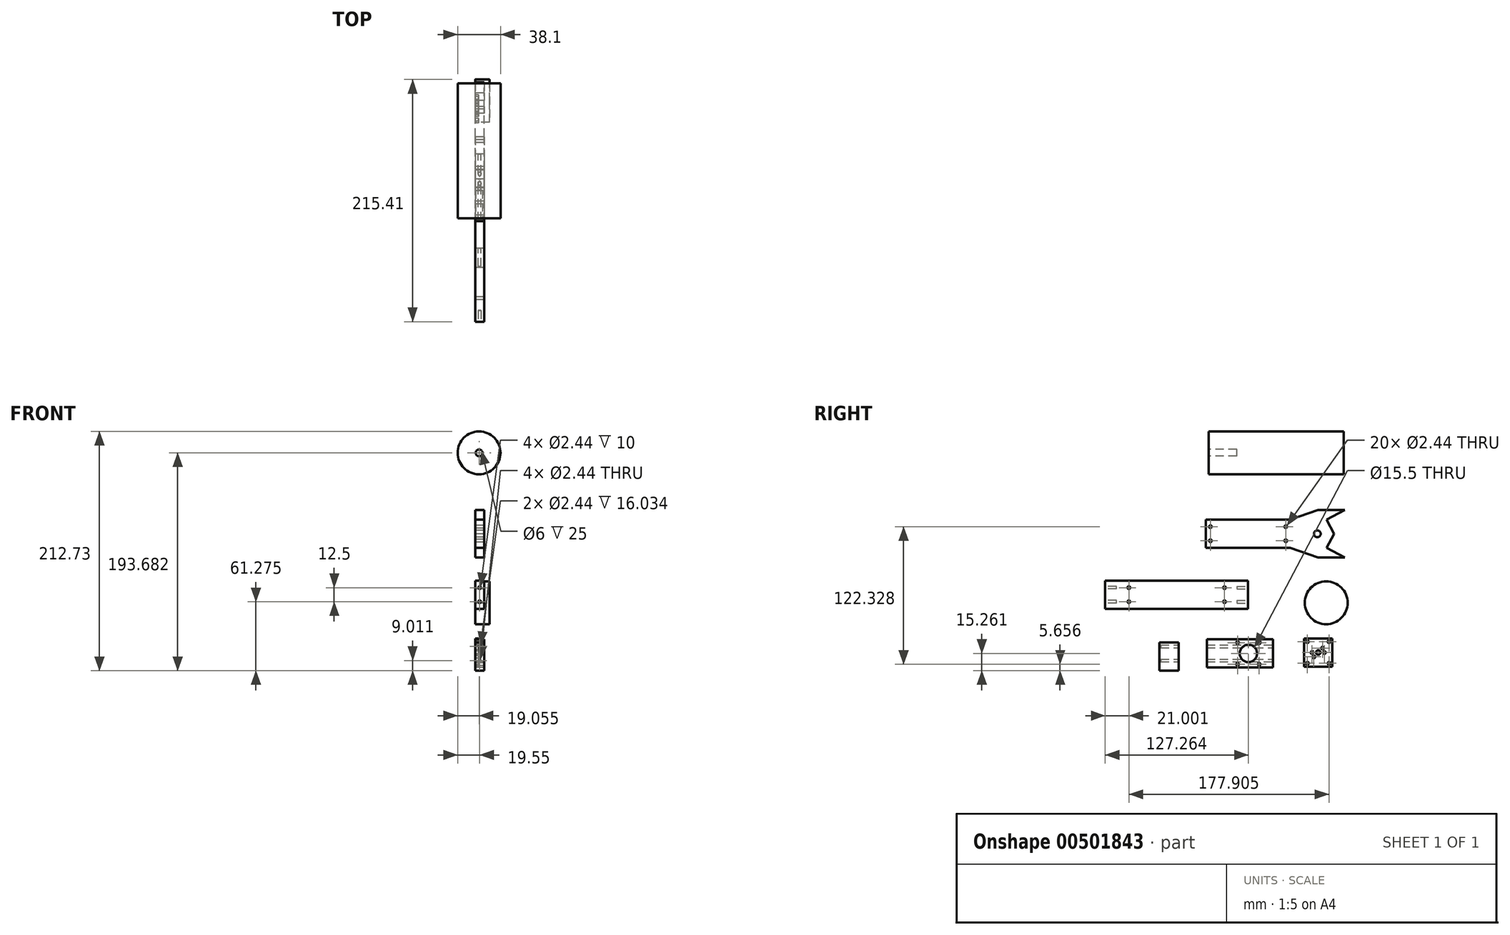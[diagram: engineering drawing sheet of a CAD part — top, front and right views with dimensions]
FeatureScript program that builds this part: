
annotation { "Feature Type Name" : "Feature", "Feature Type Description" : "" }
export const myFeature = defineFeature(function(context is Context, id is Id, definition is map)
    precondition{}
    {
        {
            var Q0;
            Q0=qCreatedBy(makeId("Right.planeOp"),FACE);
            var sketch = newSketch(context, id + "F0", { "sketchPlane" : qUnion([Q0])});
            skLineSegment(sketch, "E0", {"start": v(-2.43, 11.31) * mm, "end": v(-2.43, -13.69) * mm});
            skLineSegment(sketch, "E1", {"start": v(-2.43, -13.69) * mm, "end": v(72.57, -13.69) * mm});
            skLineSegment(sketch, "E2", {"start": v(72.57, 11.31) * mm, "end": v(-2.43, 11.31) * mm});
            skCircle(sketch, "E3", {"center": v(1.57, 5.06) * mm, "radius": 1.22 * mm});
            skCircle(sketch, "E4", {"center": v(1.57, -7.44) * mm, "radius": 1.22 * mm});
            skCircle(sketch, "E5", {"center": v(68.57, 5.06) * mm, "radius": 1.22 * mm});
            skCircle(sketch, "E6", {"center": v(68.57, -7.44) * mm, "radius": 1.22 * mm});
            skCircle(sketch, "E7", {"center": v(96.58, -1.29) * mm, "radius": 3 * mm});
            skLineSegment(sketch, "E8", {"start": v(120.9, 31.46) * mm, "end": v(120.9, -36.2) * mm});
            skLineSegment(sketch, "E9", {"start": v(72.57, 11.31) * mm, "end": v(97.18, 19.85) * mm});
            skLineSegment(sketch, "E10", {"start": v(72.57, -13.69) * mm, "end": v(97.22, -22.36) * mm});
            skLineSegment(sketch, "E11", {"start": v(97.18, 19.85) * mm, "end": v(120.9, 19.85) * mm});
            skLineSegment(sketch, "E12", {"start": v(97.22, -22.36) * mm, "end": v(120.9, -22.36) * mm});
            skLineSegment(sketch, "E13", {"start": v(120.9, 19.85) * mm, "end": v(104.74, 11.3) * mm});
            skLineSegment(sketch, "E14", {"start": v(104.74, 11.3) * mm, "end": v(111.58, -1.29) * mm});
            skLineSegment(sketch, "E15", {"start": v(120.9, -22.36) * mm, "end": v(104.74, -13.78) * mm});
            skLineSegment(sketch, "E16", {"start": v(111.58, -1.29) * mm, "end": v(104.74, -13.78) * mm});
            skSolve(sketch);
        }
        {
            var Q0;
            Q0=makeQuery(id+"F0.imprint","IMPRINT",FACE,{"disambiguationData":[TD([[makeQuery(id+"F0.imprint","IMPRINT",EDGE,{"derivedFrom":sQuery(id+"F0.wireOp",EDGE,"E0")}),1.0]])]});
            var Q1;
            Q1=makeQuery(id+"F0.imprint","IMPRINT",FACE,{"disambiguationData":[TD([[makeQuery(id+"F0.imprint","IMPRINT",EDGE,{"derivedFrom":sQuery(id+"F0.wireOp",EDGE,"7be34ed3-0eaf-4511-ae4f-23863d348a8b")}),1.0]])]});
            extrude(context, id + "F1", {"entities" : qUnion([Q0, Q1]), "depth" : 8 * mm});
        }
        {
            var Q0;
            Q0=qCreatedBy(makeId("Right.planeOp"),FACE);
            var sketch = newSketch(context, id + "F2", { "sketchPlane" : qUnion([Q0])});
            skLineSegment(sketch, "E17", {"start": v(-91.93, -42.9) * mm, "end": v(-91.93, -67.9) * mm});
            skLineSegment(sketch, "E18", {"start": v(-91.93, -42.9) * mm, "end": v(35.07, -42.9) * mm});
            skLineSegment(sketch, "E19", {"start": v(35.07, -42.9) * mm, "end": v(35.07, -67.9) * mm});
            skLineSegment(sketch, "E20", {"start": v(35.07, -67.9) * mm, "end": v(-91.93, -67.9) * mm});
            skCircle(sketch, "E21", {"center": v(-70.93, -49.14) * mm, "radius": 1.22 * mm});
            skCircle(sketch, "E22", {"center": v(-70.93, -61.64) * mm, "radius": 1.22 * mm});
            skPoint(sketch, "E23.endSnap0", {"position": v(35.07, -55.4) * mm});
            skCircle(sketch, "E24", {"center": v(14.07, -49.14) * mm, "radius": 1.22 * mm});
            skCircle(sketch, "E25", {"center": v(14.07, -61.64) * mm, "radius": 1.22 * mm});
            skSolve(sketch);
        }
        {
            var Q0;
            Q0=makeQuery(id+"F2.imprint","IMPRINT",FACE,{"disambiguationData":[TD([[makeQuery(id+"F2.imprint","IMPRINT",EDGE,{"derivedFrom":sQuery(id+"F2.wireOp",EDGE,"E17")}),1.0]])]});
            extrude(context, id + "F3", {"entities" : qUnion([Q0]), "depth" : 8 * mm});
        }
        {
            var Q0;
            Q0=qCreatedBy(makeId("Right.planeOp"),FACE);
            var sketch = newSketch(context, id + "F4", { "sketchPlane" : qUnion([Q0])});
            skCircle(sketch, "E26", {"center": v(104.43, -62.58) * mm, "radius": 19.05 * mm});
            skSolve(sketch);
        }
        {
            var Q0;
            Q0=makeQuery(id+"F4.imprint","IMPRINT",FACE,{"disambiguationData":[TD([[makeQuery(id+"F4.imprint","IMPRINT",EDGE,{"derivedFrom":sQuery(id+"F4.wireOp",EDGE,"E26")}),1.0]])]});
            extrude(context, id + "F5", {"entities" : qUnion([Q0]), "depth" : 12.7 * mm});
        }
        {
            var Q0;
            Q0=qCreatedBy(makeId("Right.planeOp"),FACE);
            var sketch = newSketch(context, id + "F6", { "sketchPlane" : qUnion([Q0])});
            skLineSegment(sketch, "E27", {"start": v(-43.63, -97.92) * mm, "end": v(-43.63, -122.92) * mm});
            skLineSegment(sketch, "E28", {"start": v(-43.63, -122.92) * mm, "end": v(-26.63, -122.92) * mm});
            skLineSegment(sketch, "E29", {"start": v(-26.63, -122.92) * mm, "end": v(-26.63, -97.92) * mm});
            skLineSegment(sketch, "E30", {"start": v(-26.63, -97.92) * mm, "end": v(-43.63, -97.92) * mm});
            skSolve(sketch);
        }
        {
            var Q0;
            Q0=qCreatedBy(makeId("Right.planeOp"),FACE);
            var sketch = newSketch(context, id + "F7", { "sketchPlane" : qUnion([Q0])});
            skLineSegment(sketch, "E31", {"start": v(-1.67, -95.16) * mm, "end": v(-1.67, -120.16) * mm});
            skLineSegment(sketch, "E32", {"start": v(-1.67, -120.16) * mm, "end": v(57.33, -120.16) * mm});
            skLineSegment(sketch, "E33", {"start": v(57.33, -120.16) * mm, "end": v(57.33, -95.16) * mm});
            skLineSegment(sketch, "E34", {"start": v(57.33, -95.16) * mm, "end": v(-1.67, -95.16) * mm});
            skCircle(sketch, "E35", {"center": v(35.33, -107.66) * mm, "radius": 7.75 * mm});
            skCircle(sketch, "E36", {"center": v(25.73, -98.05) * mm, "radius": 1.22 * mm});
            skCircle(sketch, "E37", {"center": v(44.94, -98.05) * mm, "radius": 1.22 * mm});
            skCircle(sketch, "E38", {"center": v(44.94, -117.26) * mm, "radius": 1.22 * mm});
            skCircle(sketch, "E39", {"center": v(25.73, -117.26) * mm, "radius": 1.22 * mm});
            skSolve(sketch);
        }
        {
            var Q0;
            Q0=makeQuery(id+"F6.imprint","IMPRINT",FACE,{"disambiguationData":[TD([[makeQuery(id+"F6.imprint","IMPRINT",EDGE,{"derivedFrom":sQuery(id+"F6.wireOp",EDGE,"E27")}),1.0]])]});
            extrude(context, id + "F8", {"entities" : qUnion([Q0]), "depth" : 8 * mm});
        }
        {
            var Q0;
            Q0=makeQuery(id+"F7.imprint","IMPRINT",FACE,{"disambiguationData":[TD([[makeQuery(id+"F7.imprint","IMPRINT",EDGE,{"derivedFrom":sQuery(id+"F7.wireOp",EDGE,"E31")}),1.0]])]});
            extrude(context, id + "F9", {"entities" : qUnion([Q0]), "depth" : 8 * mm});
        }
        {
            var Q0;
            Q0=qCreatedBy(makeId("Front.planeOp"),FACE);
            var sketch = newSketch(context, id + "F10", { "sketchPlane" : qUnion([Q0])});
            skCircle(sketch, "E40", {"center": v(3.5, 70.76) * mm, "radius": 19.05 * mm});
            skSolve(sketch);
        }
        {
            var Q0;
            Q0=makeQuery(id+"F10.imprint","IMPRINT",FACE,{"disambiguationData":[TD([[makeQuery(id+"F10.imprint","IMPRINT",EDGE,{"derivedFrom":sQuery(id+"F10.wireOp",EDGE,"E40")}),1.0]])]});
            extrude(context, id + "F11", {"entities" : qUnion([Q0]), "oppositeDirection" : true, "depth" : 120 * mm});
        }
        {
            var Q0;
            Q0=makeQuery(id+"F3.opExtrude","SWEPT_FACE",FACE,{"disambiguationData":[OSD([sQuery(id+"F2.wireOp",EDGE,"E19")])]});
            var sketch = newSketch(context, id + "F12", { "sketchPlane" : qUnion([Q0])});
            skCircle(sketch, "E41", {"center": v(-4, -49.14) * mm, "radius": 1.22 * mm});
            skCircle(sketch, "E42", {"center": v(-4, -61.64) * mm, "radius": 1.22 * mm});
            skSolve(sketch);
        }
        {
            var Q0;
            Q0=makeQuery(id+"F12.imprint","IMPRINT",FACE,{"disambiguationData":[TD([[makeQuery(id+"F12.imprint","IMPRINT",EDGE,{"derivedFrom":sQuery(id+"F12.wireOp",EDGE,"E41")}),1.0]])]});
            var Q1;
            Q1=makeQuery(id+"F12.imprint","IMPRINT",FACE,{"disambiguationData":[TD([[makeQuery(id+"F12.imprint","IMPRINT",EDGE,{"derivedFrom":sQuery(id+"F12.wireOp",EDGE,"E42")}),1.0]])]});
            extrude(context, id + "F13", {"entities" : qUnion([Q0, Q1]), "operationType" : NewBodyOperationType.REMOVE, "oppositeDirection" : true, "depth" : 10 * mm});
        }
        {
            var Q0;
            Q0=makeQuery(id+"F3.opExtrude","SWEPT_FACE",FACE,{"disambiguationData":[OSD([sQuery(id+"F2.wireOp",EDGE,"E17")])]});
            var sketch = newSketch(context, id + "F14", { "sketchPlane" : qUnion([Q0])});
            skCircle(sketch, "E43", {"center": v(4, -49.14) * mm, "radius": 1.22 * mm});
            skCircle(sketch, "E44", {"center": v(4, -61.64) * mm, "radius": 1.22 * mm});
            skSolve(sketch);
        }
        {
            var Q0;
            Q0=makeQuery(id+"F14.imprint","IMPRINT",FACE,{"disambiguationData":[TD([[makeQuery(id+"F14.imprint","IMPRINT",EDGE,{"derivedFrom":sQuery(id+"F14.wireOp",EDGE,"E43")}),1.0]])]});
            var Q1;
            Q1=makeQuery(id+"F14.imprint","IMPRINT",FACE,{"disambiguationData":[TD([[makeQuery(id+"F14.imprint","IMPRINT",EDGE,{"derivedFrom":sQuery(id+"F14.wireOp",EDGE,"E44")}),1.0]])]});
            extrude(context, id + "F15", {"entities" : qUnion([Q0, Q1]), "operationType" : NewBodyOperationType.REMOVE, "oppositeDirection" : true, "depth" : 10 * mm});
        }
        {
            var Q0;
            Q0=makeQuery(id+"F9.opExtrude","SWEPT_FACE",FACE,{"disambiguationData":[OSD([sQuery(id+"F7.wireOp",EDGE,"E33")])]});
            var sketch = newSketch(context, id + "F16", { "sketchPlane" : qUnion([Q0])});
            skCircle(sketch, "E45", {"center": v(-4, -101.4) * mm, "radius": 1.22 * mm});
            skCircle(sketch, "E46", {"center": v(-4, -113.9) * mm, "radius": 1.22 * mm});
            skSolve(sketch);
        }
        {
            var Q0;
            Q0=makeQuery(id+"F16.imprint","IMPRINT",FACE,{"disambiguationData":[TD([[makeQuery(id+"F16.imprint","IMPRINT",EDGE,{"derivedFrom":sQuery(id+"F16.wireOp",EDGE,"E45")}),1.0]])]});
            var Q1;
            Q1=makeQuery(id+"F16.imprint","IMPRINT",FACE,{"disambiguationData":[TD([[makeQuery(id+"F16.imprint","IMPRINT",EDGE,{"derivedFrom":sQuery(id+"F16.wireOp",EDGE,"E46")}),1.0]])]});
            extrude(context, id + "F17", {"entities" : qUnion([Q0, Q1]), "operationType" : NewBodyOperationType.REMOVE, "oppositeDirection" : true, "depth" : 100 * mm});
        }
        {
            var Q0;
            Q0=qCreatedBy(makeId("Right.planeOp"),FACE);
            var sketch = newSketch(context, id + "F18", { "sketchPlane" : qUnion([Q0])});
            skLineSegment(sketch, "E47.bottom", {"start": v(109.87, -119.32) * mm, "end": v(84.87, -119.32) * mm});
            skLineSegment(sketch, "E47.top", {"start": v(109.87, -94.32) * mm, "end": v(84.87, -94.32) * mm});
            skLineSegment(sketch, "E47.left", {"start": v(109.87, -119.32) * mm, "end": v(109.87, -94.32) * mm});
            skLineSegment(sketch, "E47.right", {"start": v(84.87, -119.32) * mm, "end": v(84.87, -94.32) * mm});
            skPoint(sketch, "E47.middle", {"position": v(97.37, -106.82) * mm});
            skCircle(sketch, "E48", {"center": v(97.37, -106.82) * mm, "radius": 2 * mm});
            skCircle(sketch, "E49", {"center": v(101.26, -102.93) * mm, "radius": 1.22 * mm});
            skCircle(sketch, "E50", {"center": v(93.48, -110.7) * mm, "radius": 1.22 * mm});
            skCircle(sketch, "E51", {"center": v(106.98, -97.22) * mm, "radius": 1.22 * mm});
            skCircle(sketch, "E52", {"center": v(87.77, -97.22) * mm, "radius": 1.22 * mm});
            skCircle(sketch, "E53", {"center": v(87.77, -116.43) * mm, "radius": 1.22 * mm});
            skCircle(sketch, "E54", {"center": v(106.98, -116.43) * mm, "radius": 1.22 * mm});
            skCircle(sketch, "E55", {"center": v(102.87, -106.82) * mm, "radius": 1.22 * mm});
            skCircle(sketch, "E56", {"center": v(91.87, -106.82) * mm, "radius": 1.22 * mm});
            skSolve(sketch);
        }
        {
            var Q0;
            Q0=makeQuery(id+"F18.imprint","IMPRINT",FACE,{"disambiguationData":[TD([[makeQuery(id+"F18.imprint","IMPRINT",EDGE,{"derivedFrom":sQuery(id+"F18.wireOp",EDGE,"E47.bottom")}),-1.0]])]});
            extrude(context, id + "F19", {"entities" : qUnion([Q0]), "depth" : 3 * mm});
        }
        {
            var Q0;
            Q0=makeQuery(id+"F11.opExtrude","CAP_FACE",FACE,{"disambiguationData":[OSD([sQuery(id+"F10.wireOp",EDGE,"E40")])],"isStart":true});
            var sketch = newSketch(context, id + "F20", { "sketchPlane" : qUnion([Q0])});
            skCircle(sketch, "E57", {"center": v(3.5, 70.76) * mm, "radius": 3 * mm});
            skSolve(sketch);
        }
        {
            var Q0;
            Q0=makeQuery(id+"F20.imprint","IMPRINT",FACE,{"disambiguationData":[TD([[makeQuery(id+"F20.imprint","IMPRINT",EDGE,{"derivedFrom":sQuery(id+"F20.wireOp",EDGE,"E57")}),1.0]])]});
            extrude(context, id + "F21", {"entities" : qUnion([Q0]), "operationType" : NewBodyOperationType.REMOVE, "oppositeDirection" : true, "depth" : 25 * mm});
        }
    });
